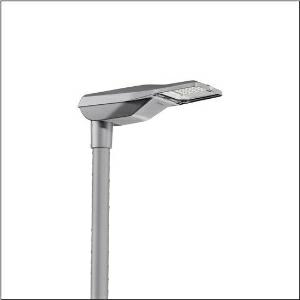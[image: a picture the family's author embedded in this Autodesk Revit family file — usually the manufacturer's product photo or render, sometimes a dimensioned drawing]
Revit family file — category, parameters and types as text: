
# Revit family: streetlight_sl_21_iq_micro___stw1_0a_5xe1e61g08cb_7f5e
name_source: partatom
category: Lighting Fixtures
units: mm (PartAtom-declared; Revit-internal decimal feet)

## family parameters
Cut with Voids When Loaded = No
Host = Face
Light Source = No
Part Type = Normal
Room Calculation Point = No
Round Connector Dimension = Use Diameter
Shared = No

## types (1)
- --- (1 x LED, 2570 lm, 19.4 W, 2700K)
    Apparent Load = 19 VA
    CIE Flux Codes = 38 75 98 100 100
    Color Rendering = 70
    Color Temperature = 2700K
    Default Elevation = 1800 mm
    Description = Streetlight SL 21 iQ micro, mast luminaire, primary light control with lens, of PMMA, primary optical cover: cover, of toughened safety glass, transparent, light distribution: STW1.0a, light emission: direct distribution, primary light characteristic: asymmetric, installation type: post-top, side-entry, LED, High Power LED, rated luminous flux: 2.570lm, luminous efficacy: 133lm/W, light colour: 727, colour temperature: 2700K, control gear: iQ Street-Remote, control: Street-Remote, Auto-Match, Temp-Guard, Lumen-Switch, Night-Set, Smart-Wire, Light-Fading, Desk-Remote (wireless, voltage-free reading and setting of iQ features in the workshop via application-optimized NFC function/RFID function), optimised constant luminous flux control (CLO 2.0), pre-setting: linear dimming characteristic, mains connection: 220..240V, AC, 50/60Hz, start of lifetime: 19W, end of service life: 20W, reduction: 10W, luminaire housing, of diecast aluminium, powder-coated, SITECO metallic grey (DB 702S), corrosivity category C5 high according to DIN EN ISO 12944, please order mast flange separately, inclination adjustable: 0°, 5°, 10°, 15°, sealing non-destructively replaceable, multi-level sealing system, length: 528mm, width: 235mm, height: 110mm, mast flange for spigot size: 42mm (side-entry): 5XC10008XM4, 60/48mm (side-entry/post-top): 5XC10108XM2, 76/60mm (side-entry/post-top): 5XC10108XM1, protection rating (complete): IP66, insulation class (complete): insulation class II (safety insulation), certification: CE, ENEC, ENEC+, VDE, impact resistance: IK10, permissible operating ambient temperature for outdoor applications: -40..+50°C, standard-compliant lighting for roads and squares, packaging unit: 1 piece

Light Distribution: STW1.0a
    Height = 110 mm
    Lamp = 1 x LED
    Lamp Light Flux = 2570 lm
    Lamp Power = 19.4 W
    Lamp count = 1
    Length = 528 mm
    Luminous efficacy = 132 lm/W
    Manufacturer = Siteco
    ModVariant = No
    Model = 5XE1E61G08CB
    Number of Poles = 1
    OnlyDefault = Yes
    Power Factor = 1
    Product Name = Streetlight SL 21 iQ micro | STW1.0a
    Product group = mast luminaire | pylon top
    ProductGroupID = 6100
    Protection Class = Protection class II
    Protection Degree = IP 66
    RLX_Detail_Level = 1
    RLX_Emergency_Light_Flux = 0 lm
    RLX_Emergency_Type = 0
    RLX_Emergency_Type_DB = No
    RlxData = <blob elided: 98717 chars, md5=32f6dc81>
    Socket = socket
    Standby Power = 0 W
    System Light Flux = 2570 lm
    System Power = 19 W
    Type Comments = factory setting: luminous flux: 100 % | dim-lin: 254 | 387 mA
    Type Image = l_1006881.jpg
    URL = http://relux.com
    VarID = @adj_138211
    Voltage = 0 V
    Weight = 0.00 kg
    Width = 235 mm

## geometry (parser evidence)
native form markers: Blend x4, Sweep x10
no freeform markers — native parametric forms only
